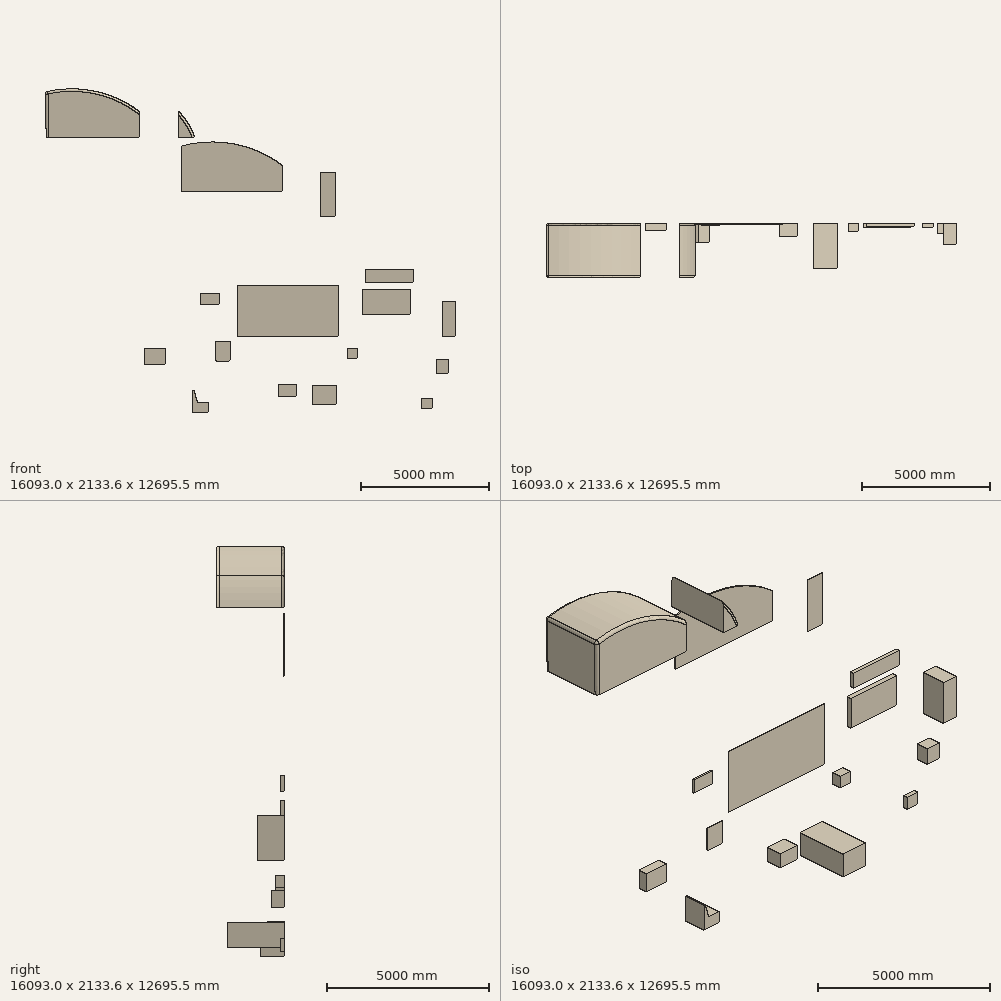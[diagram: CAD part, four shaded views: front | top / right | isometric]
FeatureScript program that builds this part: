
annotation { "Feature Type Name" : "Feature", "Feature Type Description" : "" }
export const myFeature = defineFeature(function(context is Context, id is Id, definition is map)
    precondition{}
    {
        {
            var Q0;
            Q0=qCreatedBy(makeId("Front.planeOp"),FACE);
            var sketch = newSketch(context, id + "F0", { "sketchPlane" : qUnion([Q0])});
            skLineSegment(sketch, "E0", {"start": v(1651.98, 2771.2) * mm, "end": v(3531.58, 2771.2) * mm});
            skLineSegment(sketch, "E1", {"start": v(3531.58, 2771.2) * mm, "end": v(3531.58, 1780.6) * mm});
            skLineSegment(sketch, "E2.bottom", {"start": v(-3258.92, 2935.16) * mm, "end": v(703.48, 2935.16) * mm});
            skLineSegment(sketch, "E2.top", {"start": v(-3258.92, 903.16) * mm, "end": v(703.48, 903.16) * mm});
            skLineSegment(sketch, "E2.left", {"start": v(-3258.92, 2935.16) * mm, "end": v(-3258.92, 903.16) * mm});
            skLineSegment(sketch, "E2.right", {"start": v(703.48, 2935.16) * mm, "end": v(703.48, 903.16) * mm});
            skLineSegment(sketch, "E3.bottom", {"start": v(5300.39, 2308.83) * mm, "end": v(4773.34, 2308.83) * mm});
            skLineSegment(sketch, "E3.top", {"start": v(5300.39, 937.23) * mm, "end": v(4773.34, 937.23) * mm});
            skLineSegment(sketch, "E3.left", {"start": v(5300.39, 2308.83) * mm, "end": v(5300.39, 937.23) * mm});
            skLineSegment(sketch, "E3.right", {"start": v(4773.34, 2308.83) * mm, "end": v(4773.34, 937.23) * mm});
            skLineSegment(sketch, "E4.bottom", {"start": v(4549.63, 0) * mm, "end": v(5044.93, 0) * mm});
            skLineSegment(sketch, "E4.top", {"start": v(4549.63, -523.88) * mm, "end": v(5044.93, -523.88) * mm});
            skLineSegment(sketch, "E4.left", {"start": v(4549.63, 0) * mm, "end": v(4549.63, -523.88) * mm});
            skLineSegment(sketch, "E4.right", {"start": v(5044.93, 0) * mm, "end": v(5044.93, -523.88) * mm});
            skLineSegment(sketch, "E5", {"start": v(-5455.57, 6621.97) * mm, "end": v(-1493.17, 6621.97) * mm});
            skLineSegment(sketch, "E6", {"start": v(-5455.57, 6621.97) * mm, "end": v(-5455.57, 8393.68) * mm});
            skLineSegment(sketch, "E7.bottom", {"start": v(3967.18, -1500.63) * mm, "end": v(4396.95, -1500.63) * mm});
            skLineSegment(sketch, "E7.top", {"start": v(3967.18, -1900.68) * mm, "end": v(4396.95, -1900.68) * mm});
            skLineSegment(sketch, "E7.left", {"start": v(3967.18, -1500.63) * mm, "end": v(3967.18, -1900.68) * mm});
            skLineSegment(sketch, "E7.right", {"start": v(4396.95, -1500.63) * mm, "end": v(4396.95, -1900.68) * mm});
            skLineSegment(sketch, "E8.bottom", {"start": v(-4722.42, 2600.84) * mm, "end": v(-3980.74, 2600.84) * mm});
            skLineSegment(sketch, "E8.top", {"start": v(-4722.42, 2163.96) * mm, "end": v(-3980.74, 2163.96) * mm});
            skLineSegment(sketch, "E8.left", {"start": v(-4722.42, 2600.84) * mm, "end": v(-4722.42, 2163.96) * mm});
            skLineSegment(sketch, "E8.right", {"start": v(-3980.74, 2600.84) * mm, "end": v(-3980.74, 2163.96) * mm});
            skLineSegment(sketch, "E9", {"start": v(-1493.17, 6621.97) * mm, "end": v(-1493.17, 7637.97) * mm});
            skLineSegment(sketch, "E10.bottom", {"start": v(-4131.53, 719.16) * mm, "end": v(-3521.93, 719.16) * mm});
            skLineSegment(sketch, "E10.top", {"start": v(-4080.73, -42.84) * mm, "end": v(-3572.73, -42.84) * mm});
            skLineSegment(sketch, "E10.left", {"start": v(-4131.53, 719.16) * mm, "end": v(-4131.53, 7.96) * mm});
            skLineSegment(sketch, "E10.right", {"start": v(-3521.93, 719.16) * mm, "end": v(-3521.93, 7.96) * mm});
            skPoint(sketch, "E11.visualSharp", {"position": v(-4131.53, -42.84) * mm});
            skArc(sketch, "E11.filletArc", {"start": v(-4131.53, 7.96) * mm, "mid": v(-4116.65, -27.96) * mm, "end": v(-4080.73, -42.84) * mm});
            skPoint(sketch, "E12.visualSharp", {"position": v(-3521.93, -42.84) * mm});
            skArc(sketch, "E12.filletArc", {"start": v(-3572.73, -42.84) * mm, "mid": v(-3536.81, -27.96) * mm, "end": v(-3521.93, 7.96) * mm});
            skLineSegment(sketch, "E13", {"start": v(-4955.4, -1211.26) * mm, "end": v(-4828.4, -1668.46) * mm});
            skLineSegment(sketch, "E14", {"start": v(-4828.4, -1668.46) * mm, "end": v(-4396.6, -1668.46) * mm});
            skLineSegment(sketch, "E15", {"start": v(-4396.6, -1668.46) * mm, "end": v(-4396.6, -2049.46) * mm});
            skLineSegment(sketch, "E16", {"start": v(-4396.6, -2049.46) * mm, "end": v(-4955.4, -2049.46) * mm});
            skLineSegment(sketch, "E17", {"start": v(-4955.4, -1211.26) * mm, "end": v(-5006.2, -1211.26) * mm});
            skLineSegment(sketch, "E18", {"start": v(-5006.2, -1211.26) * mm, "end": v(-5006.2, -2049.46) * mm});
            skLineSegment(sketch, "E19", {"start": v(-5006.2, -2049.46) * mm, "end": v(-4955.4, -2049.46) * mm});
            skArc(sketch, "E20", {"start": v(-1493.17, 7637.97) * mm, "mid": v(-3386.11, 8478.6) * mm, "end": v(-5455.57, 8393.68) * mm});
            skLineSegment(sketch, "E21", {"start": v(-10768.25, 8745.67) * mm, "end": v(-7110.65, 8745.67) * mm});
            skLineSegment(sketch, "E22", {"start": v(-7110.65, 8745.67) * mm, "end": v(-7110.65, 9761.67) * mm});
            skArc(sketch, "E23", {"start": v(-7110.65, 9761.67) * mm, "mid": v(-8866.94, 10555.09) * mm, "end": v(-10793.85, 10522.13) * mm});
            skLineSegment(sketch, "E24", {"start": v(10812, 947.89) * mm, "end": v(10812, -1185.71) * mm});
            skLineSegment(sketch, "E25", {"start": v(10812, -1185.71) * mm, "end": v(11626.42, -118.91) * mm});
            skLineSegment(sketch, "E26", {"start": v(11626.42, -118.91) * mm, "end": v(10812, 947.89) * mm});
            skLineSegment(sketch, "E27.bottom", {"start": v(0, 7368.13) * mm, "end": v(609.6, 7368.13) * mm});
            skLineSegment(sketch, "E27.top", {"start": v(0, 5640.93) * mm, "end": v(609.6, 5640.93) * mm});
            skLineSegment(sketch, "E27.left", {"start": v(0, 7368.13) * mm, "end": v(0, 5640.93) * mm});
            skLineSegment(sketch, "E27.right", {"start": v(609.6, 7368.13) * mm, "end": v(609.6, 5640.93) * mm});
            skLineSegment(sketch, "E28", {"start": v(1053.17, 463.62) * mm, "end": v(1459.57, 463.62) * mm});
            skLineSegment(sketch, "E29", {"start": v(1459.57, 463.62) * mm, "end": v(1459.57, 76.27) * mm});
            skLineSegment(sketch, "E30", {"start": v(1459.57, 76.27) * mm, "end": v(1053.17, 76.27) * mm});
            skLineSegment(sketch, "E31", {"start": v(1053.17, 76.27) * mm, "end": v(1053.17, 463.62) * mm});
            skLineSegment(sketch, "E32", {"start": v(-293.05, -1000.6) * mm, "end": v(621.35, -1000.6) * mm});
            skLineSegment(sketch, "E33", {"start": v(621.35, -1000.6) * mm, "end": v(621.35, -1762.6) * mm});
            skLineSegment(sketch, "E34", {"start": v(621.35, -1762.6) * mm, "end": v(-293.05, -1762.6) * mm});
            skLineSegment(sketch, "E35", {"start": v(-293.05, -1762.6) * mm, "end": v(-293.05, -1000.6) * mm});
            skLineSegment(sketch, "E36", {"start": v(-1636.37, -955.65) * mm, "end": v(-925.17, -955.65) * mm});
            skLineSegment(sketch, "E37", {"start": v(-925.17, -955.65) * mm, "end": v(-925.17, -1425.55) * mm});
            skLineSegment(sketch, "E38", {"start": v(-925.17, -1425.55) * mm, "end": v(-1636.37, -1425.55) * mm});
            skLineSegment(sketch, "E39", {"start": v(-1636.37, -1425.55) * mm, "end": v(-1636.37, -955.65) * mm});
            skLineSegment(sketch, "E40.top", {"start": v(-5568.8, 8745.67) * mm, "end": v(-4931.22, 8745.67) * mm});
            skLineSegment(sketch, "E40.left", {"start": v(-5568.8, 9761.67) * mm, "end": v(-5568.8, 8745.67) * mm});
            skArc(sketch, "E41", {"start": v(-4931.22, 8745.67) * mm, "mid": v(-5196.69, 9287.13) * mm, "end": v(-5568.8, 9761.67) * mm});
            skLineSegment(sketch, "E42", {"start": v(-10793.85, 10522.13) * mm, "end": v(-10768.25, 8745.67) * mm});
            skLineSegment(sketch, "E43", {"start": v(-15492.7, 8028.54) * mm, "end": v(-11835.1, 8028.54) * mm});
            skLineSegment(sketch, "E44", {"start": v(-11835.1, 8028.54) * mm, "end": v(-11835.1, 9044.54) * mm});
            skArc(sketch, "E45", {"start": v(-11835.1, 9044.54) * mm, "mid": v(-13877.1, 10065.19) * mm, "end": v(-16159.16, 10003.76) * mm});
            skLineSegment(sketch, "E46", {"start": v(1651.98, 1780.6) * mm, "end": v(3531.58, 1780.6) * mm});
            skLineSegment(sketch, "E47", {"start": v(1651.98, 2771.2) * mm, "end": v(1651.98, 1780.6) * mm});
            skLineSegment(sketch, "E48", {"start": v(-6101.2, 436.28) * mm, "end": v(-6101.2, -173.32) * mm});
            skLineSegment(sketch, "E49", {"start": v(-6101.2, 436.28) * mm, "end": v(-6912.91, 436.28) * mm});
            skLineSegment(sketch, "E50", {"start": v(-6101.2, -173.32) * mm, "end": v(-6914, -173.32) * mm});
            skLineSegment(sketch, "E51", {"start": v(-6912.91, 436.28) * mm, "end": v(-6914, -173.32) * mm});
            skPoint(sketch, "E52", {"position": v(-6507.06, 130.76) * mm});
            skLineSegment(sketch, "E53.bottom", {"start": v(1782.15, 3554.8) * mm, "end": v(3661.75, 3554.8) * mm});
            skLineSegment(sketch, "E53.top", {"start": v(1782.15, 3059.5) * mm, "end": v(3661.75, 3059.5) * mm});
            skLineSegment(sketch, "E53.left", {"start": v(1782.15, 3554.8) * mm, "end": v(1782.15, 3059.5) * mm});
            skLineSegment(sketch, "E53.right", {"start": v(3661.75, 3554.8) * mm, "end": v(3661.75, 3059.5) * mm});
            skLineSegment(sketch, "E54", {"start": v(-15492.7, 8028.54) * mm, "end": v(-15949.9, 8942.94) * mm});
            skLineSegment(sketch, "E55", {"start": v(-15949.9, 10057) * mm, "end": v(-15949.9, 8942.94) * mm});
            skSolve(sketch);
        }
        {
            var Q0;
            Q0=makeQuery(id+"F0.imprint","IMPRINT",FACE,{"disambiguationData":[TD([[makeQuery(id+"F0.imprint","IMPRINT",EDGE,{"derivedFrom":sQuery(id+"F0.wireOp",EDGE,"E2.bottom")}),-1.0]])]});
            extrude(context, id + "F1", {"entities" : qUnion([Q0]), "depth" : 19.05 * mm});
        }
        {
            var Q0;
            Q0=makeQuery(id+"F0.imprint","IMPRINT",FACE,{"disambiguationData":[TD([[makeQuery(id+"F0.imprint","IMPRINT",EDGE,{"derivedFrom":sQuery(id+"F0.wireOp",EDGE,"E3.bottom")}),1.0]])]});
            extrude(context, id + "F2", {"entities" : qUnion([Q0]), "depth" : 838.2 * mm});
        }
        {
            var Q0;
            Q0=makeQuery(id+"F0.imprint","IMPRINT",FACE,{"disambiguationData":[TD([[makeQuery(id+"F0.imprint","IMPRINT",EDGE,{"derivedFrom":sQuery(id+"F0.wireOp",EDGE,"E4.bottom")}),-1.0]])]});
            extrude(context, id + "F3", {"entities" : qUnion([Q0]), "depth" : 406.4 * mm});
        }
        {
            var Q0;
            Q0=makeQuery(id+"F0.imprint","IMPRINT",FACE,{"disambiguationData":[TD([[makeQuery(id+"F0.imprint","IMPRINT",EDGE,{"derivedFrom":sQuery(id+"F0.wireOp",EDGE,"E7.bottom")}),-1.0]])]});
            extrude(context, id + "F4", {"entities" : qUnion([Q0]), "depth" : 152.4 * mm});
        }
        {
            var Q0;
            Q0=makeQuery(id+"F0.imprint","IMPRINT",FACE,{"disambiguationData":[TD([[makeQuery(id+"F0.imprint","IMPRINT",EDGE,{"derivedFrom":sQuery(id+"F0.wireOp",EDGE,"E8.bottom")}),-1.0]])]});
            extrude(context, id + "F5", {"entities" : qUnion([Q0]), "depth" : 76.2 * mm});
        }
        {
            var Q0;
            Q0=makeQuery(id+"F0.imprint","IMPRINT",FACE,{"disambiguationData":[TD([[makeQuery(id+"F0.imprint","IMPRINT",EDGE,{"derivedFrom":sQuery(id+"F0.wireOp",EDGE,"E5")}),1.0]])]});
            extrude(context, id + "F6", {"entities" : qUnion([Q0]), "depth" : 50.8 * mm});
        }
        {
            var Q0;
            Q0=makeQuery(id+"F0.imprint","IMPRINT",FACE,{"disambiguationData":[TD([[makeQuery(id+"F0.imprint","IMPRINT",EDGE,{"derivedFrom":sQuery(id+"F0.wireOp",EDGE,"E10.bottom")}),-1.0]])]});
            extrude(context, id + "F7", {"entities" : qUnion([Q0]), "depth" : 19.05 * mm});
        }
        {
            var Q0;
            Q0=makeQuery(id+"F0.imprint","IMPRINT",FACE,{"disambiguationData":[TD([[makeQuery(id+"F0.imprint","IMPRINT",EDGE,{"derivedFrom":sQuery(id+"F0.wireOp",EDGE,"E13")}),-1.0]])]});
            extrude(context, id + "F8", {"entities" : qUnion([Q0]), "depth" : 762 * mm, "offsetDistance" : 25.4 * mm});
        }
        {
            var Q0;
            Q0=makeQuery(id+"F0.imprint","IMPRINT",FACE,{"disambiguationData":[TD([[makeQuery(id+"F0.imprint","IMPRINT",EDGE,{"derivedFrom":sQuery(id+"F0.wireOp",EDGE,"E21")}),1.0]])]});
            extrude(context, id + "F9", {"entities" : qUnion([Q0]), "depth" : 2133.6 * mm});
        }
        {
            var Q0;
            Q0=makeQuery(id+"F0.imprint","IMPRINT",FACE,{"disambiguationData":[TD([[makeQuery(id+"F0.imprint","IMPRINT",EDGE,{"derivedFrom":sQuery(id+"F0.wireOp",EDGE,"E27.bottom")}),-1.0]])]});
            extrude(context, id + "F10", {"entities" : qUnion([Q0]), "depth" : 25.4 * mm});
        }
        {
            var Q0;
            Q0=makeQuery(id+"F0.imprint","IMPRINT",FACE,{"disambiguationData":[TD([[makeQuery(id+"F0.imprint","IMPRINT",EDGE,{"derivedFrom":sQuery(id+"F0.wireOp",EDGE,"E28")}),-1.0]])]});
            extrude(context, id + "F11", {"entities" : qUnion([Q0]), "depth" : 304.8 * mm, "offsetDistance" : 25.4 * mm});
        }
        {
            var Q0;
            Q0=makeQuery(id+"F0.imprint","IMPRINT",FACE,{"disambiguationData":[TD([[makeQuery(id+"F0.imprint","IMPRINT",EDGE,{"derivedFrom":sQuery(id+"F0.wireOp",EDGE,"E32")}),-1.0]])]});
            extrude(context, id + "F12", {"entities" : qUnion([Q0]), "depth" : 1778 * mm, "offsetDistance" : 25.4 * mm});
        }
        {
            var Q0;
            Q0=makeQuery(id+"F0.imprint","IMPRINT",FACE,{"disambiguationData":[TD([[makeQuery(id+"F0.imprint","IMPRINT",EDGE,{"derivedFrom":sQuery(id+"F0.wireOp",EDGE,"E36")}),-1.0]])]});
            extrude(context, id + "F13", {"entities" : qUnion([Q0]), "depth" : 533.4 * mm, "offsetDistance" : 25.4 * mm});
        }
        {
            var Q0;
            Q0=makeQuery(id+"F0.imprint","IMPRINT",FACE,{"disambiguationData":[TD([[makeQuery(id+"F0.imprint","IMPRINT",EDGE,{"derivedFrom":sQuery(id+"F0.wireOp",EDGE,"E40.top")}),1.0]])]});
            extrude(context, id + "F14", {"entities" : qUnion([Q0]), "depth" : 2133.6 * mm, "offsetDistance" : 25.4 * mm});
        }
        {
            var Q0;
            Q0=makeQuery(id+"F9.opExtrude","SWEPT_EDGE",EDGE,{"disambiguationData":[OSD([sQuery(id+"F0.wireOp",EDGE,"E23"),sQuery(id+"F0.wireOp",EDGE,"E42")])]});
            fillet(context, id + "F15", {"entities" : qUnion([Q0]), "radius" : 105.48 * mm, "tangentPropagation" : true, "allowEdgeOverflow" : false});
        }
        {
            var Q0;
            Q0=makeQuery(id+"F9.opExtrude","CAP_EDGE",EDGE,{"disambiguationData":[OSD([sQuery(id+"F0.wireOp",EDGE,"E42")])],"isStart":false});
            var Q1;
            Q1=makeQuery(id+"F9.opExtrude","CAP_EDGE",EDGE,{"disambiguationData":[OSD([sQuery(id+"F0.wireOp",EDGE,"E42")])],"isStart":true});
            var Q2;
            Q2=makeQuery(id+"F14.opExtrude","CAP_EDGE",EDGE,{"disambiguationData":[OSD([sQuery(id+"F0.wireOp",EDGE,"E41")])],"isStart":false});
            var Q3;
            Q3=makeQuery(id+"F14.opExtrude","CAP_EDGE",EDGE,{"disambiguationData":[OSD([sQuery(id+"F0.wireOp",EDGE,"E41")])],"isStart":true});
            fillet(context, id + "F16", {"entities" : qUnion([Q0, Q1, Q2, Q3]), "radius" : 101.6 * mm, "tangentPropagation" : true, "allowEdgeOverflow" : false});
        }
        {
            var Q0;
            Q0=makeQuery(id+"F0.imprint","IMPRINT",FACE,{"disambiguationData":[TD([[makeQuery(id+"F0.imprint","IMPRINT",EDGE,{"derivedFrom":sQuery(id+"F0.wireOp",EDGE,"E0")}),-1.0]])]});
            extrude(context, id + "F17", {"entities" : qUnion([Q0]), "depth" : 152.4 * mm, "offsetDistance" : 25.4 * mm});
        }
        {
            var Q0;
            Q0=makeQuery(id+"F0.imprint","IMPRINT",FACE,{"disambiguationData":[TD([[makeQuery(id+"F0.imprint","IMPRINT",EDGE,{"derivedFrom":sQuery(id+"F0.wireOp",EDGE,"E48")}),-1.0]])]});
            extrude(context, id + "F18", {"entities" : qUnion([Q0]), "depth" : 292.1 * mm, "offsetDistance" : 25.4 * mm});
        }
        {
            var Q0;
            Q0=makeQuery(id+"F0.imprint","IMPRINT",FACE,{"disambiguationData":[TD([[makeQuery(id+"F0.imprint","IMPRINT",EDGE,{"derivedFrom":sQuery(id+"F0.wireOp",EDGE,"E53.bottom")}),-1.0]])]});
            extrude(context, id + "F19", {"entities" : qUnion([Q0]), "depth" : 127 * mm, "offsetDistance" : 25.4 * mm});
        }
    });
